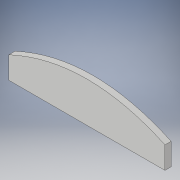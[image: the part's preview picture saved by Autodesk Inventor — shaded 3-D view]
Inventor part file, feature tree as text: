
AUTODESK INVENTOR PART (.ipt)
format: ipt  version: 2018 (Build 220112000, 112)  size: 98,816 bytes
history: native  units: in
note: dims shown in document units (in); Inventor stores cm internally (conversion verified against a paired STEP export)
features: extrude x1, sketch x1
ambient origin geometry x8: Origin, YZ Plane, XZ Plane, XY Plane, X Axis, Y Axis, Z Axis, Center Point
bodies: Solid1 (feature_tree)
feature tree (2):
  extrude  "Extrusion1"  Depth=5.0in
  sketch  "Sketch2"  dims[d5=5.0in d6=5.0in d7=0.3937in d8=0.0in]
